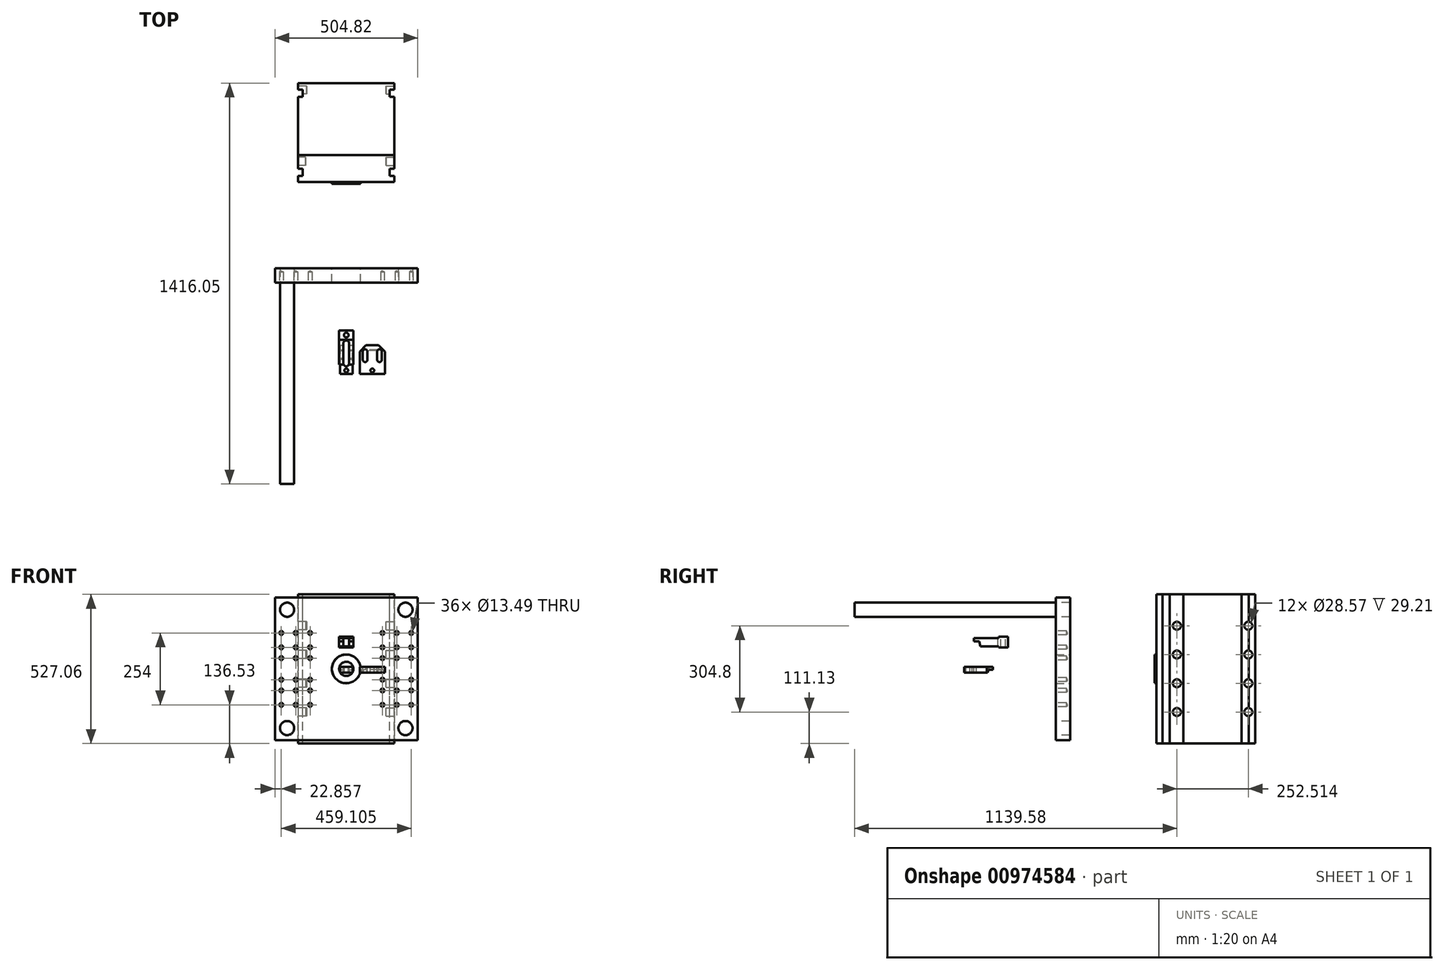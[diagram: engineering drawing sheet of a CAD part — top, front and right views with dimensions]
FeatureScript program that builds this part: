
annotation { "Feature Type Name" : "Feature", "Feature Type Description" : "" }
export const myFeature = defineFeature(function(context is Context, id is Id, definition is map)
    precondition{}
    {
        {
            var Q0;
            Q0=qCreatedBy(makeId("Front.planeOp"),FACE);
            var sketch = newSketch(context, id + "F0", { "sketchPlane" : qUnion([Q0])});
            skLineSegment(sketch, "E0.bottom", {"start": v(-252.41, 252.41) * mm, "end": v(252.41, 252.41) * mm});
            skLineSegment(sketch, "E0.top", {"start": v(-252.41, -252.41) * mm, "end": v(252.41, -252.41) * mm});
            skLineSegment(sketch, "E0.left", {"start": v(-252.41, 252.41) * mm, "end": v(-252.41, -252.41) * mm});
            skLineSegment(sketch, "E0.right", {"start": v(252.41, 252.41) * mm, "end": v(252.41, -252.41) * mm});
            skPoint(sketch, "E0.middle", {"position": v(0, 0) * mm});
            skSolve(sketch);
        }
        {
            var Q0;
            Q0=makeQuery(id+"F0.imprint","IMPRINT",FACE,{"disambiguationData":[TD([[makeQuery(id+"F0.imprint","IMPRINT",EDGE,{"derivedFrom":sQuery(id+"F0.wireOp",EDGE,"E0.bottom")}),-1.0]])]});
            extrude(context, id + "F1", {"entities" : qUnion([Q0]), "depth" : 50.8 * mm, "offsetDistance" : 25.4 * mm});
        }
        {
            var Q0;
            Q0=makeQuery(id+"F1.opExtrude","CAP_FACE",FACE,{"disambiguationData":[OSD([sQuery(id+"F0.wireOp",EDGE,"E0.bottom"),sQuery(id+"F0.wireOp",EDGE,"E0.top"),sQuery(id+"F0.wireOp",EDGE,"E0.left"),sQuery(id+"F0.wireOp",EDGE,"E0.right")])],"isStart":false});
            var sketch = newSketch(context, id + "F2", { "sketchPlane" : qUnion([Q0])});
            skLineSegment(sketch, "E1.bottom", {"start": v(-209.14, 209.14) * mm, "end": v(209.14, 209.14) * mm, "construction": true});
            skLineSegment(sketch, "E1.top", {"start": v(-209.14, -209.14) * mm, "end": v(209.14, -209.14) * mm, "construction": true});
            skLineSegment(sketch, "E1.left", {"start": v(-209.14, 209.14) * mm, "end": v(-209.14, -209.14) * mm, "construction": true});
            skLineSegment(sketch, "E1.right", {"start": v(209.14, 209.14) * mm, "end": v(209.14, -209.14) * mm, "construction": true});
            skPoint(sketch, "E1.middle", {"position": v(0, 0) * mm});
            skCircle(sketch, "E2", {"center": v(-209.14, 209.14) * mm, "radius": 25.02 * mm});
            skCircle(sketch, "E3", {"center": v(209.14, 209.14) * mm, "radius": 25.02 * mm});
            skCircle(sketch, "E4", {"center": v(209.14, -209.14) * mm, "radius": 25.02 * mm});
            skCircle(sketch, "E5", {"center": v(-209.14, -209.14) * mm, "radius": 25.02 * mm});
            skSolve(sketch);
        }
        {
            var Q0;
            Q0=makeQuery(id+"F2.imprint","IMPRINT",FACE,{"disambiguationData":[TD([[makeQuery(id+"F2.imprint","IMPRINT",EDGE,{"derivedFrom":sQuery(id+"F2.wireOp",EDGE,"E2")}),1.0]])]});
            var Q1;
            Q1=makeQuery(id+"F2.imprint","IMPRINT",FACE,{"disambiguationData":[TD([[makeQuery(id+"F2.imprint","IMPRINT",EDGE,{"derivedFrom":sQuery(id+"F2.wireOp",EDGE,"E3")}),1.0]])]});
            var Q2;
            Q2=makeQuery(id+"F2.imprint","IMPRINT",FACE,{"disambiguationData":[TD([[makeQuery(id+"F2.imprint","IMPRINT",EDGE,{"derivedFrom":sQuery(id+"F2.wireOp",EDGE,"E5")}),1.0]])]});
            var Q3;
            Q3=makeQuery(id+"F2.imprint","IMPRINT",FACE,{"disambiguationData":[TD([[makeQuery(id+"F2.imprint","IMPRINT",EDGE,{"derivedFrom":sQuery(id+"F2.wireOp",EDGE,"E4")}),1.0]])]});
            extrude(context, id + "F3", {"entities" : qUnion([Q0, Q1, Q2, Q3]), "operationType" : NewBodyOperationType.REMOVE, "endBound" : BoundingType.THROUGH_ALL, "oppositeDirection" : true, "depth" : 25.4 * mm, "offsetDistance" : 25.4 * mm});
        }
        {
            var Q0;
            Q0=makeQuery(id+"F1.opExtrude","CAP_FACE",FACE,{"disambiguationData":[OSD([sQuery(id+"F0.wireOp",EDGE,"E0.bottom"),sQuery(id+"F0.wireOp",EDGE,"E0.top"),sQuery(id+"F0.wireOp",EDGE,"E0.left"),sQuery(id+"F0.wireOp",EDGE,"E0.right")])],"isStart":false});
            var sketch = newSketch(context, id + "F4", { "sketchPlane" : qUnion([Q0])});
            skPoint(sketch, "E6", {"position": v(229.55, 38.1) * mm});
            skPoint(sketch, "E7", {"position": v(178.75, 38.1) * mm});
            skPoint(sketch, "E8", {"position": v(127.95, 38.1) * mm});
            skPoint(sketch, "E9", {"position": v(229.55, 76.2) * mm});
            skPoint(sketch, "E10", {"position": v(229.55, 127) * mm});
            skPoint(sketch, "E11", {"position": v(178.75, 76.2) * mm});
            skPoint(sketch, "E12", {"position": v(178.75, 127) * mm});
            skPoint(sketch, "E13", {"position": v(127.95, 76.2) * mm});
            skPoint(sketch, "E14", {"position": v(127.95, 127) * mm});
            skPoint(sketch, "E15.MirrorP", {"position": v(127.95, -38.1) * mm});
            skPoint(sketch, "E16.MirrorP", {"position": v(178.75, -38.1) * mm});
            skPoint(sketch, "E17.MirrorP", {"position": v(229.55, -38.1) * mm});
            skPoint(sketch, "E18.MirrorP", {"position": v(229.55, -76.2) * mm});
            skPoint(sketch, "E19.MirrorP", {"position": v(178.75, -76.2) * mm});
            skPoint(sketch, "E20.MirrorP", {"position": v(127.95, -76.2) * mm});
            skPoint(sketch, "E21.MirrorP", {"position": v(127.95, -127) * mm});
            skPoint(sketch, "E22.MirrorP", {"position": v(178.75, -127) * mm});
            skPoint(sketch, "E23.MirrorP", {"position": v(229.55, -127) * mm});
            skPoint(sketch, "E24.MirrorP", {"position": v(-127.95, -38.1) * mm});
            skPoint(sketch, "E25.MirrorP", {"position": v(-127.95, -76.2) * mm});
            skPoint(sketch, "E26.MirrorP", {"position": v(-127.95, -127) * mm});
            skPoint(sketch, "E27.MirrorP", {"position": v(-178.75, -127) * mm});
            skPoint(sketch, "E28.MirrorP", {"position": v(-178.75, -76.2) * mm});
            skPoint(sketch, "E29.MirrorP", {"position": v(-178.75, -38.1) * mm});
            skPoint(sketch, "E30.MirrorP", {"position": v(-229.55, -38.1) * mm});
            skPoint(sketch, "E31.MirrorP", {"position": v(-229.55, -76.2) * mm});
            skPoint(sketch, "E32.MirrorP", {"position": v(-229.55, -127) * mm});
            skPoint(sketch, "E33.MirrorP", {"position": v(-229.55, 38.1) * mm});
            skPoint(sketch, "E34.MirrorP", {"position": v(-229.55, 76.2) * mm});
            skPoint(sketch, "E35.MirrorP", {"position": v(-229.55, 127) * mm});
            skPoint(sketch, "E36.MirrorP", {"position": v(-178.75, 127) * mm});
            skPoint(sketch, "E37.MirrorP", {"position": v(-178.75, 76.2) * mm});
            skPoint(sketch, "E38.MirrorP", {"position": v(-178.75, 38.1) * mm});
            skPoint(sketch, "E39.MirrorP", {"position": v(-127.95, 38.1) * mm});
            skPoint(sketch, "E40.MirrorP", {"position": v(-127.95, 76.2) * mm});
            skPoint(sketch, "E41.MirrorP", {"position": v(-127.95, 127) * mm});
            skSolve(sketch);
        }
        {
            var Q0;
            Q0=sQuery(id+"F4.wireOp",VERTEX,"E35.MirrorP");
            var Q1;
            Q1=sQuery(id+"F4.wireOp",VERTEX,"E34.MirrorP");
            var Q2;
            Q2=sQuery(id+"F4.wireOp",VERTEX,"E33.MirrorP");
            var Q3;
            Q3=sQuery(id+"F4.wireOp",VERTEX,"E38.MirrorP");
            var Q4;
            Q4=sQuery(id+"F4.wireOp",VERTEX,"E37.MirrorP");
            var Q5;
            Q5=sQuery(id+"F4.wireOp",VERTEX,"E36.MirrorP");
            var Q6;
            Q6=sQuery(id+"F4.wireOp",VERTEX,"E41.MirrorP");
            var Q7;
            Q7=sQuery(id+"F4.wireOp",VERTEX,"E40.MirrorP");
            var Q8;
            Q8=sQuery(id+"F4.wireOp",VERTEX,"E39.MirrorP");
            var Q9;
            Q9=sQuery(id+"F4.wireOp",VERTEX,"E24.MirrorP");
            var Q10;
            Q10=sQuery(id+"F4.wireOp",VERTEX,"E29.MirrorP");
            var Q11;
            Q11=sQuery(id+"F4.wireOp",VERTEX,"E30.MirrorP");
            var Q12;
            Q12=sQuery(id+"F4.wireOp",VERTEX,"E31.MirrorP");
            var Q13;
            Q13=sQuery(id+"F4.wireOp",VERTEX,"E28.MirrorP");
            var Q14;
            Q14=sQuery(id+"F4.wireOp",VERTEX,"E25.MirrorP");
            var Q15;
            Q15=sQuery(id+"F4.wireOp",VERTEX,"E26.MirrorP");
            var Q16;
            Q16=sQuery(id+"F4.wireOp",VERTEX,"E27.MirrorP");
            var Q17;
            Q17=sQuery(id+"F4.wireOp",VERTEX,"E32.MirrorP");
            var Q18;
            Q18=sQuery(id+"F4.wireOp",VERTEX,"E21.MirrorP");
            var Q19;
            Q19=sQuery(id+"F4.wireOp",VERTEX,"E22.MirrorP");
            var Q20;
            Q20=sQuery(id+"F4.wireOp",VERTEX,"E23.MirrorP");
            var Q21;
            Q21=sQuery(id+"F4.wireOp",VERTEX,"E18.MirrorP");
            var Q22;
            Q22=sQuery(id+"F4.wireOp",VERTEX,"E19.MirrorP");
            var Q23;
            Q23=sQuery(id+"F4.wireOp",VERTEX,"E20.MirrorP");
            var Q24;
            Q24=sQuery(id+"F4.wireOp",VERTEX,"E15.MirrorP");
            var Q25;
            Q25=sQuery(id+"F4.wireOp",VERTEX,"E16.MirrorP");
            var Q26;
            Q26=sQuery(id+"F4.wireOp",VERTEX,"E17.MirrorP");
            var Q27;
            Q27=sQuery(id+"F4.wireOp",VERTEX,"E6");
            var Q28;
            Q28=sQuery(id+"F4.wireOp",VERTEX,"E7");
            var Q29;
            Q29=sQuery(id+"F4.wireOp",VERTEX,"E8");
            var Q30;
            Q30=sQuery(id+"F4.wireOp",VERTEX,"E13");
            var Q31;
            Q31=sQuery(id+"F4.wireOp",VERTEX,"E11");
            var Q32;
            Q32=sQuery(id+"F4.wireOp",VERTEX,"E9");
            var Q33;
            Q33=sQuery(id+"F4.wireOp",VERTEX,"E10");
            var Q34;
            Q34=sQuery(id+"F4.wireOp",VERTEX,"E12");
            var Q35;
            Q35=sQuery(id+"F4.wireOp",VERTEX,"E14");
            var Q36;
            Q36=makeQuery(id+"F1.opExtrude","SWEPT_BODY",BODY,{"disambiguationData":[OSD([sQuery(id+"F0.wireOp",EDGE,"E0.bottom"),sQuery(id+"F0.wireOp",EDGE,"E0.top"),sQuery(id+"F0.wireOp",EDGE,"E0.left"),sQuery(id+"F0.wireOp",EDGE,"E0.right")])]});
            hole(context, id + "F5", {"style" : HoleStyle.SIMPLE, "endStyle" : HoleEndStyle.BLIND, "standardTappedOrClearance" : lookupTablePath({ "standard" : "ANSI", "engagement" : "75%", "pitch" : "11 tpi", "size" : "5/8", "type" : "Tapped" }), "standardBlindInLast" : lookupTablePath({ "standard" : "ANSI", "fit" : "Free", "engagement" : "75%", "pitch" : "11 tpi", "size" : "5/8", "type" : "Clearance & tapped" }), "holeDiameter" : 13.5 * mm, "majorDiameter" : 15.88 * mm, "showTappedDepth" : true, "holeDepth" : 38.1 * mm, "isTappedThrough" : true, "tappedDepth" : 31.17 * mm, "tapClearance" : 3, "startFromSketch" : true, "locations" : qUnion([Q0, Q1, Q2, Q3, Q4, Q5, Q6, Q7, Q8, Q9, Q10, Q11, Q12, Q13, Q14, Q15, Q16, Q17, Q18, Q19, Q20, Q21, Q22, Q23, Q24, Q25, Q26, Q27, Q28, Q29, Q30, Q31, Q32, Q33, Q34, Q35]), "scope" : qUnion([Q36])});
        }
        {
            var Q0;
            Q0=makeQuery(id+"F1.opExtrude","CAP_FACE",FACE,{"disambiguationData":[OSD([sQuery(id+"F0.wireOp",EDGE,"E0.bottom"),sQuery(id+"F0.wireOp",EDGE,"E0.top"),sQuery(id+"F0.wireOp",EDGE,"E0.left"),sQuery(id+"F0.wireOp",EDGE,"E0.right")])],"isStart":false});
            var sketch = newSketch(context, id + "F6", { "sketchPlane" : qUnion([Q0])});
            skCircle(sketch, "E42.0", {"center": v(-209.14, 209.14) * mm, "radius": 25.02 * mm});
            skSolve(sketch);
        }
        {
            var Q0;
            Q0=makeQuery(id+"F6.imprint","IMPRINT",FACE,{"disambiguationData":[TD([[makeQuery(id+"F6.imprint","IMPRINT",EDGE,{"derivedFrom":sQuery(id+"F6.wireOp",EDGE,"E42.0")}),1.0]])]});
            extrude(context, id + "F7", {"entities" : qUnion([Q0]), "depth" : 711.2 * mm, "offsetDistance" : 25.4 * mm});
        }
        {
            var Q0;
            Q0=qCreatedBy(makeId("Right.planeOp"),FACE);
            var sketch = newSketch(context, id + "F8", { "sketchPlane" : qUnion([Q0])});
            skLineSegment(sketch, "E43.bottom", {"start": v(304.8, 263.53) * mm, "end": v(400.05, 263.53) * mm});
            skLineSegment(sketch, "E43.top", {"start": v(304.8, -263.52) * mm, "end": v(400.05, -263.52) * mm});
            skLineSegment(sketch, "E43.left", {"start": v(304.8, 263.53) * mm, "end": v(304.8, -263.52) * mm});
            skLineSegment(sketch, "E43.right", {"start": v(400.05, 263.53) * mm, "end": v(400.05, -263.52) * mm});
            skPoint(sketch, "E43.middle", {"position": v(352.43, 0) * mm});
            skSolve(sketch);
        }
        {
            var Q0;
            Q0=makeQuery(id+"F8.imprint","IMPRINT",FACE,{"disambiguationData":[TD([[makeQuery(id+"F8.imprint","IMPRINT",EDGE,{"derivedFrom":sQuery(id+"F8.wireOp",EDGE,"E43.bottom")}),-1.0]])]});
            extrude(context, id + "F9", {"entities" : qUnion([Q0]), "endBound" : BoundingType.SYMMETRIC, "depth" : 339.72 * mm, "offsetDistance" : 25.4 * mm});
        }
        {
            var Q0;
            Q0=makeQuery(id+"F9.opExtrude","SWEPT_FACE",FACE,{"disambiguationData":[OSD([sQuery(id+"F8.wireOp",EDGE,"E43.bottom")])]});
            var sketch = newSketch(context, id + "F10", { "sketchPlane" : qUnion([Q0])});
            skLineSegment(sketch, "E44.bottom", {"start": v(169.86, 327.03) * mm, "end": v(153.86, 327.03) * mm});
            skLineSegment(sketch, "E44.top", {"start": v(169.86, 352.43) * mm, "end": v(153.86, 352.43) * mm});
            skLineSegment(sketch, "E44.left", {"start": v(169.86, 327.03) * mm, "end": v(169.86, 352.43) * mm});
            skLineSegment(sketch, "E44.right", {"start": v(153.86, 327.03) * mm, "end": v(153.86, 352.43) * mm});
            skLineSegment(sketch, "E45", {"start": v(0, 400.05) * mm, "end": v(0, 304.8) * mm, "construction": true});
            skLineSegment(sketch, "E46.MirrorCS", {"start": v(-153.86, 327.03) * mm, "end": v(-153.86, 352.43) * mm});
            skLineSegment(sketch, "E47.MirrorCS", {"start": v(-169.86, 352.43) * mm, "end": v(-153.86, 352.43) * mm});
            skLineSegment(sketch, "E48.MirrorCS", {"start": v(-169.86, 327.03) * mm, "end": v(-169.86, 352.43) * mm});
            skLineSegment(sketch, "E49.MirrorCS", {"start": v(-169.86, 327.03) * mm, "end": v(-153.86, 327.03) * mm});
            skSolve(sketch);
        }
        {
            var Q0;
            Q0=makeQuery(id+"F10.imprint","IMPRINT",FACE,{"disambiguationData":[TD([[makeQuery(id+"F10.imprint","IMPRINT",EDGE,{"derivedFrom":sQuery(id+"F10.wireOp",EDGE,"E46.MirrorCS")}),1.0]])]});
            var Q1;
            Q1=makeQuery(id+"F10.imprint","IMPRINT",FACE,{"disambiguationData":[TD([[makeQuery(id+"F10.imprint","IMPRINT",EDGE,{"derivedFrom":sQuery(id+"F10.wireOp",EDGE,"E44.bottom")}),-1.0]])]});
            extrude(context, id + "F11", {"entities" : qUnion([Q0, Q1]), "operationType" : NewBodyOperationType.REMOVE, "endBound" : BoundingType.THROUGH_ALL, "oppositeDirection" : true, "depth" : 25.4 * mm, "offsetDistance" : 25.4 * mm});
        }
        {
            var Q0;
            {var subQ0=sQuery(id+"F8.wireOp",EDGE,"E43.bottom");var subQ1=sQuery(id+"F8.wireOp",EDGE,"E43.right");var subQ2=sQuery(id+"F8.wireOp",EDGE,"E43.top");Q0=makeQuery(id+"F11.boolean.opBoolean","SPLIT",FACE,{"disambiguationData":[TD([makeQuery(id+"F9.opExtrude","SWEPT_FACE",FACE,{"disambiguationData":[OSD([subQ1])]})])],"derivedFrom":makeQuery(id+"F9.opExtrude","CAP_FACE",FACE,{"disambiguationData":[OSD([subQ0,subQ2,sQuery(id+"F8.wireOp",EDGE,"E43.left"),subQ1])],"isStart":false})});}
            var sketch = newSketch(context, id + "F12", { "sketchPlane" : qUnion([Q0])});
            skCircle(sketch, "E50", {"center": v(377.58, 152.4) * mm, "radius": 14.29 * mm});
            skCircle(sketch, "E51", {"center": v(377.58, 50.8) * mm, "radius": 14.29 * mm});
            skCircle(sketch, "E52", {"center": v(377.58, -50.8) * mm, "radius": 14.29 * mm});
            skCircle(sketch, "E53", {"center": v(377.58, -152.4) * mm, "radius": 14.29 * mm});
            skLineSegment(sketch, "E54", {"start": v(377.58, 50.8) * mm, "end": v(377.58, -50.8) * mm, "construction": true});
            skPoint(sketch, "E55", {"position": v(377.58, 0) * mm});
            skSolve(sketch);
        }
        {
            var Q0;
            Q0=makeQuery(id+"F12.imprint","IMPRINT",FACE,{"disambiguationData":[TD([[makeQuery(id+"F12.imprint","IMPRINT",EDGE,{"derivedFrom":sQuery(id+"F12.wireOp",EDGE,"E50")}),1.0]])]});
            var Q1;
            Q1=makeQuery(id+"F12.imprint","IMPRINT",FACE,{"disambiguationData":[TD([[makeQuery(id+"F12.imprint","IMPRINT",EDGE,{"derivedFrom":sQuery(id+"F12.wireOp",EDGE,"E51")}),1.0]])]});
            var Q2;
            Q2=makeQuery(id+"F12.imprint","IMPRINT",FACE,{"disambiguationData":[TD([[makeQuery(id+"F12.imprint","IMPRINT",EDGE,{"derivedFrom":sQuery(id+"F12.wireOp",EDGE,"E52")}),1.0]])]});
            var Q3;
            Q3=makeQuery(id+"F12.imprint","IMPRINT",FACE,{"disambiguationData":[TD([[makeQuery(id+"F12.imprint","IMPRINT",EDGE,{"derivedFrom":sQuery(id+"F12.wireOp",EDGE,"E53")}),1.0]])]});
            extrude(context, id + "F13", {"entities" : qUnion([Q0, Q1, Q2, Q3]), "operationType" : NewBodyOperationType.REMOVE, "oppositeDirection" : true, "depth" : 29.2 * mm, "offsetDistance" : 25.4 * mm});
        }
        {
            var Q0;
            {var subQ0=sQuery(id+"F8.wireOp",EDGE,"E43.bottom");var subQ1=sQuery(id+"F8.wireOp",EDGE,"E43.right");var subQ2=sQuery(id+"F8.wireOp",EDGE,"E43.top");Q0=makeQuery(id+"F11.boolean.opBoolean","SPLIT",FACE,{"disambiguationData":[TD([makeQuery(id+"F9.opExtrude","SWEPT_FACE",FACE,{"disambiguationData":[OSD([subQ1])]})])],"derivedFrom":makeQuery(id+"F9.opExtrude","CAP_FACE",FACE,{"disambiguationData":[OSD([subQ0,subQ2,sQuery(id+"F8.wireOp",EDGE,"E43.left"),subQ1])],"isStart":true})});}
            var sketch = newSketch(context, id + "F14", { "sketchPlane" : qUnion([Q0])});
            skCircle(sketch, "E56.0", {"center": v(-377.58, 152.4) * mm, "radius": 14.29 * mm});
            skCircle(sketch, "E57.0", {"center": v(-377.58, 50.8) * mm, "radius": 14.29 * mm});
            skCircle(sketch, "E58.0", {"center": v(-377.58, -50.8) * mm, "radius": 14.29 * mm});
            skCircle(sketch, "E59.0", {"center": v(-377.58, -152.4) * mm, "radius": 14.29 * mm});
            skSolve(sketch);
        }
        {
            var Q0;
            Q0=makeQuery(id+"F14.imprint","IMPRINT",FACE,{"disambiguationData":[TD([[makeQuery(id+"F14.imprint","IMPRINT",EDGE,{"derivedFrom":sQuery(id+"F14.wireOp",EDGE,"E56.0")}),1.0]])]});
            var Q1;
            Q1=makeQuery(id+"F14.imprint","IMPRINT",FACE,{"disambiguationData":[TD([[makeQuery(id+"F14.imprint","IMPRINT",EDGE,{"derivedFrom":sQuery(id+"F14.wireOp",EDGE,"E57.0")}),1.0]])]});
            var Q2;
            Q2=makeQuery(id+"F14.imprint","IMPRINT",FACE,{"disambiguationData":[TD([[makeQuery(id+"F14.imprint","IMPRINT",EDGE,{"derivedFrom":sQuery(id+"F14.wireOp",EDGE,"E58.0")}),1.0]])]});
            var Q3;
            Q3=makeQuery(id+"F14.imprint","IMPRINT",FACE,{"disambiguationData":[TD([[makeQuery(id+"F14.imprint","IMPRINT",EDGE,{"derivedFrom":sQuery(id+"F14.wireOp",EDGE,"E59.0")}),1.0]])]});
            extrude(context, id + "F15", {"entities" : qUnion([Q0, Q1, Q2, Q3]), "operationType" : NewBodyOperationType.REMOVE, "oppositeDirection" : true, "depth" : 25.4 * mm, "offsetDistance" : 25.4 * mm});
        }
        {
            var Q0;
            Q0=makeQuery(id+"F9.opExtrude","SWEPT_FACE",FACE,{"disambiguationData":[OSD([sQuery(id+"F8.wireOp",EDGE,"E43.left")])]});
            var sketch = newSketch(context, id + "F16", { "sketchPlane" : qUnion([Q0])});
            skCircle(sketch, "E60", {"center": v(0, 0) * mm, "radius": 50.62 * mm});
            skCircle(sketch, "E61", {"center": v(0, 0) * mm, "radius": 25.17 * mm});
            skSolve(sketch);
        }
        {
            var Q0;
            Q0=makeQuery(id+"F16.imprint","IMPRINT",FACE,{"disambiguationData":[TD([[makeQuery(id+"F16.imprint","IMPRINT",EDGE,{"derivedFrom":sQuery(id+"F16.wireOp",EDGE,"E60")}),1.0]])]});
            extrude(context, id + "F17", {"entities" : qUnion([Q0]), "operationType" : NewBodyOperationType.ADD, "depth" : 6.35 * mm, "offsetDistance" : 25.4 * mm});
        }
        {
            var Q0;
            Q0=makeQuery(id+"F9.opExtrude","SWEPT_FACE",FACE,{"disambiguationData":[OSD([sQuery(id+"F8.wireOp",EDGE,"E43.right")])]});
            var sketch = newSketch(context, id + "F18", { "sketchPlane" : qUnion([Q0])});
            skLineSegment(sketch, "E62.bottom", {"start": v(-169.86, 263.53) * mm, "end": v(169.86, 263.53) * mm});
            skLineSegment(sketch, "E62.top", {"start": v(-169.86, -263.52) * mm, "end": v(169.86, -263.52) * mm});
            skLineSegment(sketch, "E62.left", {"start": v(-169.86, 263.53) * mm, "end": v(-169.86, -263.52) * mm});
            skLineSegment(sketch, "E62.right", {"start": v(169.86, 263.53) * mm, "end": v(169.86, -263.52) * mm});
            skSolve(sketch);
        }
        {
            var Q0;
            Q0=makeQuery(id+"F18.imprint","IMPRINT",FACE,{"disambiguationData":[TD([[makeQuery(id+"F18.imprint","IMPRINT",EDGE,{"derivedFrom":sQuery(id+"F18.wireOp",EDGE,"E62.bottom")}),-1.0]])]});
            extrude(context, id + "F19", {"entities" : qUnion([Q0]), "depth" : 254 * mm, "offsetDistance" : 25.4 * mm});
        }
        {
            var Q0;
            Q0=makeQuery(id+"F19.opExtrude","SWEPT_FACE",FACE,{"disambiguationData":[OSD([sQuery(id+"F18.wireOp",EDGE,"E62.bottom")])]});
            var sketch = newSketch(context, id + "F20", { "sketchPlane" : qUnion([Q0])});
            skLineSegment(sketch, "E63.bottom", {"start": v(169.86, 631.82) * mm, "end": v(153.86, 631.82) * mm});
            skLineSegment(sketch, "E63.top", {"start": v(169.86, 606.42) * mm, "end": v(153.86, 606.42) * mm});
            skLineSegment(sketch, "E63.left", {"start": v(169.86, 631.82) * mm, "end": v(169.86, 606.42) * mm});
            skLineSegment(sketch, "E63.right", {"start": v(153.86, 631.82) * mm, "end": v(153.86, 606.42) * mm});
            skLineSegment(sketch, "E64.bottom", {"start": v(-169.86, 631.82) * mm, "end": v(-153.86, 631.82) * mm});
            skLineSegment(sketch, "E64.top", {"start": v(-169.86, 606.42) * mm, "end": v(-153.86, 606.42) * mm});
            skLineSegment(sketch, "E64.left", {"start": v(-169.86, 631.82) * mm, "end": v(-169.86, 606.42) * mm});
            skLineSegment(sketch, "E64.right", {"start": v(-153.86, 631.82) * mm, "end": v(-153.86, 606.42) * mm});
            skSolve(sketch);
        }
        {
            var Q0;
            Q0=makeQuery(id+"F20.imprint","IMPRINT",FACE,{"disambiguationData":[TD([[makeQuery(id+"F20.imprint","IMPRINT",EDGE,{"derivedFrom":sQuery(id+"F20.wireOp",EDGE,"E64.bottom")}),-1.0]])]});
            var Q1;
            Q1=makeQuery(id+"F20.imprint","IMPRINT",FACE,{"disambiguationData":[TD([[makeQuery(id+"F20.imprint","IMPRINT",EDGE,{"derivedFrom":sQuery(id+"F20.wireOp",EDGE,"E63.bottom")}),1.0]])]});
            extrude(context, id + "F21", {"entities" : qUnion([Q0, Q1]), "operationType" : NewBodyOperationType.REMOVE, "endBound" : BoundingType.THROUGH_ALL, "oppositeDirection" : true, "depth" : 25.4 * mm, "offsetDistance" : 25.4 * mm});
        }
        {
            var Q0;
            {var subQ1=sQuery(id+"F18.wireOp",EDGE,"E62.left");Q0=makeQuery(id+"F21.boolean.opBoolean","SPLIT",FACE,{"disambiguationData":[TD([makeQuery(id+"F21.opExtrude","SWEPT_FACE",FACE,{"disambiguationData":[OSD([sQuery(id+"F20.wireOp",EDGE,"E63.bottom")])]})])],"derivedFrom":makeQuery(id+"F19.opExtrude","SWEPT_FACE",FACE,{"disambiguationData":[OSD([subQ1])]})});}
            var sketch = newSketch(context, id + "F22", { "sketchPlane" : qUnion([Q0])});
            skCircle(sketch, "E65", {"center": v(630.1, 152.4) * mm, "radius": 14.29 * mm});
            skCircle(sketch, "E66", {"center": v(630.1, 50.8) * mm, "radius": 14.29 * mm});
            skCircle(sketch, "E67", {"center": v(630.1, -50.8) * mm, "radius": 14.29 * mm});
            skCircle(sketch, "E68", {"center": v(630.1, -152.4) * mm, "radius": 14.29 * mm});
            skCircle(sketch, "E69.0", {"center": v(377.58, 50.8) * mm, "radius": 14.29 * mm});
            skCircle(sketch, "E70.0", {"center": v(377.58, 152.4) * mm, "radius": 14.29 * mm});
            skCircle(sketch, "E71.0", {"center": v(377.58, -50.8) * mm, "radius": 14.29 * mm});
            skCircle(sketch, "E72.0", {"center": v(377.58, -152.4) * mm, "radius": 14.29 * mm});
            skSolve(sketch);
        }
        {
            var Q0;
            {var subQ0=sQuery(id+"F22.wireOp",EDGE,"E65");var subQ1=makeQuery(id+"F21.boolean.opBoolean","COPY",EDGE,{"derivedFrom":makeQuery(id+"F21.opExtrude","SWEPT_EDGE",EDGE,{"disambiguationData":[OSD([sQuery(id+"F18.wireOp",EDGE,"E62.bottom"),sQuery(id+"F18.wireOp",EDGE,"E62.left"),sQuery(id+"F20.wireOp",EDGE,"E63.bottom"),sQuery(id+"F20.wireOp",EDGE,"E63.left")])]})});var subQ2=makeQuery(id+"F22.imprint","INTERSECT",VERTEX,{"disambiguationData":[OD(0.0)],"derivedFrom":[subQ1,subQ0]});Q0=makeQuery(id+"F22.imprint","IMPRINT",FACE,{"disambiguationData":[TD([[makeQuery(id+"F22.imprint","IMPRINT",EDGE,{"disambiguationData":[TD([[subQ2,1.0]])],"derivedFrom":subQ0}),1.0]])]});}
            var Q1;
            {var subQ0=sQuery(id+"F22.wireOp",EDGE,"E65");var subQ1=makeQuery(id+"F21.boolean.opBoolean","COPY",EDGE,{"derivedFrom":makeQuery(id+"F21.opExtrude","SWEPT_EDGE",EDGE,{"disambiguationData":[OSD([sQuery(id+"F18.wireOp",EDGE,"E62.bottom"),sQuery(id+"F18.wireOp",EDGE,"E62.left"),sQuery(id+"F20.wireOp",EDGE,"E63.bottom"),sQuery(id+"F20.wireOp",EDGE,"E63.left")])]})});var subQ2=makeQuery(id+"F22.imprint","INTERSECT",VERTEX,{"disambiguationData":[OD(0.0)],"derivedFrom":[subQ1,subQ0]});Q1=makeQuery(id+"F22.imprint","IMPRINT",FACE,{"disambiguationData":[TD([[makeQuery(id+"F22.imprint","IMPRINT",EDGE,{"disambiguationData":[TD([[subQ2,-1.0]])],"derivedFrom":subQ0}),1.0]])]});}
            var Q2;
            {var subQ0=sQuery(id+"F22.wireOp",EDGE,"E66");var subQ1=makeQuery(id+"F21.boolean.opBoolean","COPY",EDGE,{"derivedFrom":makeQuery(id+"F21.opExtrude","SWEPT_EDGE",EDGE,{"disambiguationData":[OSD([sQuery(id+"F18.wireOp",EDGE,"E62.bottom"),sQuery(id+"F18.wireOp",EDGE,"E62.left"),sQuery(id+"F20.wireOp",EDGE,"E63.bottom"),sQuery(id+"F20.wireOp",EDGE,"E63.left")])]})});var subQ2=makeQuery(id+"F22.imprint","INTERSECT",VERTEX,{"disambiguationData":[OD(0.0)],"derivedFrom":[subQ1,subQ0]});Q2=makeQuery(id+"F22.imprint","IMPRINT",FACE,{"disambiguationData":[TD([[makeQuery(id+"F22.imprint","IMPRINT",EDGE,{"disambiguationData":[TD([[subQ2,-1.0]])],"derivedFrom":subQ0}),1.0]])]});}
            var Q3;
            {var subQ0=sQuery(id+"F22.wireOp",EDGE,"E66");var subQ1=makeQuery(id+"F21.boolean.opBoolean","COPY",EDGE,{"derivedFrom":makeQuery(id+"F21.opExtrude","SWEPT_EDGE",EDGE,{"disambiguationData":[OSD([sQuery(id+"F18.wireOp",EDGE,"E62.bottom"),sQuery(id+"F18.wireOp",EDGE,"E62.left"),sQuery(id+"F20.wireOp",EDGE,"E63.bottom"),sQuery(id+"F20.wireOp",EDGE,"E63.left")])]})});var subQ2=makeQuery(id+"F22.imprint","INTERSECT",VERTEX,{"disambiguationData":[OD(0.0)],"derivedFrom":[subQ1,subQ0]});Q3=makeQuery(id+"F22.imprint","IMPRINT",FACE,{"disambiguationData":[TD([[makeQuery(id+"F22.imprint","IMPRINT",EDGE,{"disambiguationData":[TD([[subQ2,1.0]])],"derivedFrom":subQ0}),1.0]])]});}
            var Q4;
            {var subQ0=sQuery(id+"F22.wireOp",EDGE,"E67");var subQ1=makeQuery(id+"F21.boolean.opBoolean","COPY",EDGE,{"derivedFrom":makeQuery(id+"F21.opExtrude","SWEPT_EDGE",EDGE,{"disambiguationData":[OSD([sQuery(id+"F18.wireOp",EDGE,"E62.bottom"),sQuery(id+"F18.wireOp",EDGE,"E62.left"),sQuery(id+"F20.wireOp",EDGE,"E63.bottom"),sQuery(id+"F20.wireOp",EDGE,"E63.left")])]})});var subQ2=makeQuery(id+"F22.imprint","INTERSECT",VERTEX,{"disambiguationData":[OD(0.0)],"derivedFrom":[subQ1,subQ0]});Q4=makeQuery(id+"F22.imprint","IMPRINT",FACE,{"disambiguationData":[TD([[makeQuery(id+"F22.imprint","IMPRINT",EDGE,{"disambiguationData":[TD([[subQ2,1.0]])],"derivedFrom":subQ0}),1.0]])]});}
            var Q5;
            {var subQ0=sQuery(id+"F22.wireOp",EDGE,"E67");var subQ1=makeQuery(id+"F21.boolean.opBoolean","COPY",EDGE,{"derivedFrom":makeQuery(id+"F21.opExtrude","SWEPT_EDGE",EDGE,{"disambiguationData":[OSD([sQuery(id+"F18.wireOp",EDGE,"E62.bottom"),sQuery(id+"F18.wireOp",EDGE,"E62.left"),sQuery(id+"F20.wireOp",EDGE,"E63.bottom"),sQuery(id+"F20.wireOp",EDGE,"E63.left")])]})});var subQ2=makeQuery(id+"F22.imprint","INTERSECT",VERTEX,{"disambiguationData":[OD(0.0)],"derivedFrom":[subQ1,subQ0]});Q5=makeQuery(id+"F22.imprint","IMPRINT",FACE,{"disambiguationData":[TD([[makeQuery(id+"F22.imprint","IMPRINT",EDGE,{"disambiguationData":[TD([[subQ2,-1.0]])],"derivedFrom":subQ0}),1.0]])]});}
            var Q6;
            {var subQ0=sQuery(id+"F22.wireOp",EDGE,"E68");var subQ1=makeQuery(id+"F21.boolean.opBoolean","COPY",EDGE,{"derivedFrom":makeQuery(id+"F21.opExtrude","SWEPT_EDGE",EDGE,{"disambiguationData":[OSD([sQuery(id+"F18.wireOp",EDGE,"E62.bottom"),sQuery(id+"F18.wireOp",EDGE,"E62.left"),sQuery(id+"F20.wireOp",EDGE,"E63.bottom"),sQuery(id+"F20.wireOp",EDGE,"E63.left")])]})});var subQ2=makeQuery(id+"F22.imprint","INTERSECT",VERTEX,{"disambiguationData":[OD(0.0)],"derivedFrom":[subQ1,subQ0]});Q6=makeQuery(id+"F22.imprint","IMPRINT",FACE,{"disambiguationData":[TD([[makeQuery(id+"F22.imprint","IMPRINT",EDGE,{"disambiguationData":[TD([[subQ2,1.0]])],"derivedFrom":subQ0}),1.0]])]});}
            var Q7;
            {var subQ0=sQuery(id+"F22.wireOp",EDGE,"E68");var subQ1=makeQuery(id+"F21.boolean.opBoolean","COPY",EDGE,{"derivedFrom":makeQuery(id+"F21.opExtrude","SWEPT_EDGE",EDGE,{"disambiguationData":[OSD([sQuery(id+"F18.wireOp",EDGE,"E62.bottom"),sQuery(id+"F18.wireOp",EDGE,"E62.left"),sQuery(id+"F20.wireOp",EDGE,"E63.bottom"),sQuery(id+"F20.wireOp",EDGE,"E63.left")])]})});var subQ2=makeQuery(id+"F22.imprint","INTERSECT",VERTEX,{"disambiguationData":[OD(0.0)],"derivedFrom":[subQ1,subQ0]});Q7=makeQuery(id+"F22.imprint","IMPRINT",FACE,{"disambiguationData":[TD([[makeQuery(id+"F22.imprint","IMPRINT",EDGE,{"disambiguationData":[TD([[subQ2,-1.0]])],"derivedFrom":subQ0}),1.0]])]});}
            extrude(context, id + "F23", {"entities" : qUnion([Q0, Q1, Q2, Q3, Q4, Q5, Q6, Q7]), "operationType" : NewBodyOperationType.REMOVE, "oppositeDirection" : true, "depth" : 29.2 * mm, "offsetDistance" : 25.4 * mm});
        }
        {
            var Q0;
            {var subQ1=sQuery(id+"F18.wireOp",EDGE,"E62.right");Q0=makeQuery(id+"F21.boolean.opBoolean","SPLIT",FACE,{"disambiguationData":[TD([makeQuery(id+"F21.opExtrude","SWEPT_FACE",FACE,{"disambiguationData":[OSD([sQuery(id+"F20.wireOp",EDGE,"E64.bottom")])]})])],"derivedFrom":makeQuery(id+"F19.opExtrude","SWEPT_FACE",FACE,{"disambiguationData":[OSD([subQ1])]})});}
            var sketch = newSketch(context, id + "F24", { "sketchPlane" : qUnion([Q0])});
            skCircle(sketch, "E73.0.0", {"center": v(-630.1, 152.4) * mm, "radius": 14.29 * mm});
            skCircle(sketch, "E74.0.0", {"center": v(-630.1, 50.8) * mm, "radius": 14.29 * mm});
            skCircle(sketch, "E75.0.0", {"center": v(-630.1, -50.8) * mm, "radius": 14.29 * mm});
            skCircle(sketch, "E76.0.0", {"center": v(-630.1, -152.4) * mm, "radius": 14.29 * mm});
            skSolve(sketch);
        }
        {
            var Q0;
            {var subQ0=sQuery(id+"F24.wireOp",EDGE,"E73.0.0");var subQ1=makeQuery(id+"F21.boolean.opBoolean","COPY",EDGE,{"derivedFrom":makeQuery(id+"F21.opExtrude","SWEPT_EDGE",EDGE,{"disambiguationData":[OSD([sQuery(id+"F18.wireOp",EDGE,"E62.bottom"),sQuery(id+"F18.wireOp",EDGE,"E62.right"),sQuery(id+"F20.wireOp",EDGE,"E64.bottom"),sQuery(id+"F20.wireOp",EDGE,"E64.left")])]})});var subQ2=makeQuery(id+"F24.imprint","INTERSECT",VERTEX,{"disambiguationData":[OD(0.0)],"derivedFrom":[subQ1,subQ0]});Q0=makeQuery(id+"F24.imprint","IMPRINT",FACE,{"disambiguationData":[TD([[makeQuery(id+"F24.imprint","IMPRINT",EDGE,{"disambiguationData":[TD([[subQ2,-1.0]])],"derivedFrom":subQ0}),1.0]])]});}
            var Q1;
            {var subQ0=sQuery(id+"F24.wireOp",EDGE,"E74.0.0");var subQ1=makeQuery(id+"F21.boolean.opBoolean","COPY",EDGE,{"derivedFrom":makeQuery(id+"F21.opExtrude","SWEPT_EDGE",EDGE,{"disambiguationData":[OSD([sQuery(id+"F18.wireOp",EDGE,"E62.bottom"),sQuery(id+"F18.wireOp",EDGE,"E62.right"),sQuery(id+"F20.wireOp",EDGE,"E64.bottom"),sQuery(id+"F20.wireOp",EDGE,"E64.left")])]})});var subQ2=makeQuery(id+"F24.imprint","INTERSECT",VERTEX,{"disambiguationData":[OD(0.0)],"derivedFrom":[subQ1,subQ0]});Q1=makeQuery(id+"F24.imprint","IMPRINT",FACE,{"disambiguationData":[TD([[makeQuery(id+"F24.imprint","IMPRINT",EDGE,{"disambiguationData":[TD([[subQ2,-1.0]])],"derivedFrom":subQ0}),1.0]])]});}
            var Q2;
            {var subQ0=sQuery(id+"F24.wireOp",EDGE,"E74.0.0");var subQ1=makeQuery(id+"F21.boolean.opBoolean","COPY",EDGE,{"derivedFrom":makeQuery(id+"F21.opExtrude","SWEPT_EDGE",EDGE,{"disambiguationData":[OSD([sQuery(id+"F18.wireOp",EDGE,"E62.bottom"),sQuery(id+"F18.wireOp",EDGE,"E62.right"),sQuery(id+"F20.wireOp",EDGE,"E64.bottom"),sQuery(id+"F20.wireOp",EDGE,"E64.left")])]})});var subQ2=makeQuery(id+"F24.imprint","INTERSECT",VERTEX,{"disambiguationData":[OD(0.0)],"derivedFrom":[subQ1,subQ0]});Q2=makeQuery(id+"F24.imprint","IMPRINT",FACE,{"disambiguationData":[TD([[makeQuery(id+"F24.imprint","IMPRINT",EDGE,{"disambiguationData":[TD([[subQ2,1.0]])],"derivedFrom":subQ0}),1.0]])]});}
            var Q3;
            {var subQ0=sQuery(id+"F24.wireOp",EDGE,"E73.0.0");var subQ1=makeQuery(id+"F21.boolean.opBoolean","COPY",EDGE,{"derivedFrom":makeQuery(id+"F21.opExtrude","SWEPT_EDGE",EDGE,{"disambiguationData":[OSD([sQuery(id+"F18.wireOp",EDGE,"E62.bottom"),sQuery(id+"F18.wireOp",EDGE,"E62.right"),sQuery(id+"F20.wireOp",EDGE,"E64.bottom"),sQuery(id+"F20.wireOp",EDGE,"E64.left")])]})});var subQ2=makeQuery(id+"F24.imprint","INTERSECT",VERTEX,{"disambiguationData":[OD(0.0)],"derivedFrom":[subQ1,subQ0]});Q3=makeQuery(id+"F24.imprint","IMPRINT",FACE,{"disambiguationData":[TD([[makeQuery(id+"F24.imprint","IMPRINT",EDGE,{"disambiguationData":[TD([[subQ2,1.0]])],"derivedFrom":subQ0}),1.0]])]});}
            var Q4;
            {var subQ0=sQuery(id+"F24.wireOp",EDGE,"E75.0.0");var subQ1=makeQuery(id+"F21.boolean.opBoolean","COPY",EDGE,{"derivedFrom":makeQuery(id+"F21.opExtrude","SWEPT_EDGE",EDGE,{"disambiguationData":[OSD([sQuery(id+"F18.wireOp",EDGE,"E62.bottom"),sQuery(id+"F18.wireOp",EDGE,"E62.right"),sQuery(id+"F20.wireOp",EDGE,"E64.bottom"),sQuery(id+"F20.wireOp",EDGE,"E64.left")])]})});var subQ2=makeQuery(id+"F24.imprint","INTERSECT",VERTEX,{"disambiguationData":[OD(0.0)],"derivedFrom":[subQ1,subQ0]});Q4=makeQuery(id+"F24.imprint","IMPRINT",FACE,{"disambiguationData":[TD([[makeQuery(id+"F24.imprint","IMPRINT",EDGE,{"disambiguationData":[TD([[subQ2,1.0]])],"derivedFrom":subQ0}),1.0]])]});}
            var Q5;
            {var subQ0=sQuery(id+"F24.wireOp",EDGE,"E75.0.0");var subQ1=makeQuery(id+"F21.boolean.opBoolean","COPY",EDGE,{"derivedFrom":makeQuery(id+"F21.opExtrude","SWEPT_EDGE",EDGE,{"disambiguationData":[OSD([sQuery(id+"F18.wireOp",EDGE,"E62.bottom"),sQuery(id+"F18.wireOp",EDGE,"E62.right"),sQuery(id+"F20.wireOp",EDGE,"E64.bottom"),sQuery(id+"F20.wireOp",EDGE,"E64.left")])]})});var subQ2=makeQuery(id+"F24.imprint","INTERSECT",VERTEX,{"disambiguationData":[OD(0.0)],"derivedFrom":[subQ1,subQ0]});Q5=makeQuery(id+"F24.imprint","IMPRINT",FACE,{"disambiguationData":[TD([[makeQuery(id+"F24.imprint","IMPRINT",EDGE,{"disambiguationData":[TD([[subQ2,-1.0]])],"derivedFrom":subQ0}),1.0]])]});}
            var Q6;
            {var subQ0=sQuery(id+"F24.wireOp",EDGE,"E76.0.0");var subQ1=makeQuery(id+"F21.boolean.opBoolean","COPY",EDGE,{"derivedFrom":makeQuery(id+"F21.opExtrude","SWEPT_EDGE",EDGE,{"disambiguationData":[OSD([sQuery(id+"F18.wireOp",EDGE,"E62.bottom"),sQuery(id+"F18.wireOp",EDGE,"E62.right"),sQuery(id+"F20.wireOp",EDGE,"E64.bottom"),sQuery(id+"F20.wireOp",EDGE,"E64.left")])]})});var subQ2=makeQuery(id+"F24.imprint","INTERSECT",VERTEX,{"disambiguationData":[OD(0.0)],"derivedFrom":[subQ1,subQ0]});Q6=makeQuery(id+"F24.imprint","IMPRINT",FACE,{"disambiguationData":[TD([[makeQuery(id+"F24.imprint","IMPRINT",EDGE,{"disambiguationData":[TD([[subQ2,1.0]])],"derivedFrom":subQ0}),1.0]])]});}
            var Q7;
            {var subQ0=sQuery(id+"F24.wireOp",EDGE,"E76.0.0");var subQ1=makeQuery(id+"F21.boolean.opBoolean","COPY",EDGE,{"derivedFrom":makeQuery(id+"F21.opExtrude","SWEPT_EDGE",EDGE,{"disambiguationData":[OSD([sQuery(id+"F18.wireOp",EDGE,"E62.bottom"),sQuery(id+"F18.wireOp",EDGE,"E62.right"),sQuery(id+"F20.wireOp",EDGE,"E64.bottom"),sQuery(id+"F20.wireOp",EDGE,"E64.left")])]})});var subQ2=makeQuery(id+"F24.imprint","INTERSECT",VERTEX,{"disambiguationData":[OD(0.0)],"derivedFrom":[subQ1,subQ0]});Q7=makeQuery(id+"F24.imprint","IMPRINT",FACE,{"disambiguationData":[TD([[makeQuery(id+"F24.imprint","IMPRINT",EDGE,{"disambiguationData":[TD([[subQ2,-1.0]])],"derivedFrom":subQ0}),1.0]])]});}
            extrude(context, id + "F25", {"entities" : qUnion([Q0, Q1, Q2, Q3, Q4, Q5, Q6, Q7]), "operationType" : NewBodyOperationType.REMOVE, "oppositeDirection" : true, "depth" : 29.2 * mm, "offsetDistance" : 25.4 * mm});
        }
        {
            var Q0;
            Q0=makeQuery(id+"F1.opExtrude","CAP_FACE",FACE,{"disambiguationData":[OSD([sQuery(id+"F0.wireOp",EDGE,"E0.bottom"),sQuery(id+"F0.wireOp",EDGE,"E0.top"),sQuery(id+"F0.wireOp",EDGE,"E0.left"),sQuery(id+"F0.wireOp",EDGE,"E0.right")])],"isStart":true});
            var sketch = newSketch(context, id + "F26", { "sketchPlane" : qUnion([Q0])});
            skCircle(sketch, "E77", {"center": v(0, 0) * mm, "radius": 50.8 * mm});
            skSolve(sketch);
        }
        {
            var Q0;
            Q0=makeQuery(id+"F26.imprint","IMPRINT",FACE,{"disambiguationData":[TD([[makeQuery(id+"F26.imprint","IMPRINT",EDGE,{"derivedFrom":sQuery(id+"F26.wireOp",EDGE,"E77")}),1.0]])]});
            extrude(context, id + "F27", {"entities" : qUnion([Q0]), "operationType" : NewBodyOperationType.REMOVE, "endBound" : BoundingType.THROUGH_ALL, "oppositeDirection" : true, "depth" : 25.4 * mm, "offsetDistance" : 25.4 * mm});
        }
        {
            var Q0;
            Q0=qCreatedBy(makeId("Right.planeOp"),FACE);
            var sketch = newSketch(context, id + "F28", { "sketchPlane" : qUnion([Q0])});
            skLineSegment(sketch, "E78.bottom", {"start": v(-373.82, 12.7) * mm, "end": v(-272.22, 12.7) * mm});
            skLineSegment(sketch, "E78.top", {"start": v(-373.82, -12.7) * mm, "end": v(-272.22, -12.7) * mm});
            skLineSegment(sketch, "E78.left", {"start": v(-373.82, 12.7) * mm, "end": v(-373.82, -12.7) * mm});
            skLineSegment(sketch, "E78.right", {"start": v(-272.22, 12.7) * mm, "end": v(-272.22, -12.7) * mm});
            skPoint(sketch, "E78.middle", {"position": v(-323.02, 0) * mm});
            skSolve(sketch);
        }
        {
            var Q0;
            Q0=makeQuery(id+"F28.imprint","IMPRINT",FACE,{"disambiguationData":[TD([[makeQuery(id+"F28.imprint","IMPRINT",EDGE,{"derivedFrom":sQuery(id+"F28.wireOp",EDGE,"E78.bottom")}),-1.0]])]});
            extrude(context, id + "F29", {"entities" : qUnion([Q0]), "endBound" : BoundingType.SYMMETRIC, "depth" : 44.45 * mm, "offsetDistance" : 25.4 * mm});
        }
        {
            var Q0;
            Q0=makeQuery(id+"F29.opExtrude","SWEPT_FACE",FACE,{"disambiguationData":[OSD([sQuery(id+"F28.wireOp",EDGE,"E78.bottom")])]});
            var sketch = newSketch(context, id + "F30", { "sketchPlane" : qUnion([Q0])});
            skPoint(sketch, "E79", {"position": v(0, -361.12) * mm});
            skPoint(sketch, "E79.positionSnap0", {"position": v(0, -373.82) * mm});
            skSolve(sketch);
        }
        {
            var Q0;
            Q0=sQuery(id+"F30.wireOp",VERTEX,"E79");
            var Q1;
            Q1=makeQuery(id+"F29.opExtrude","SWEPT_BODY",BODY,{"disambiguationData":[OSD([sQuery(id+"F28.wireOp",EDGE,"E78.bottom"),sQuery(id+"F28.wireOp",EDGE,"E78.top"),sQuery(id+"F28.wireOp",EDGE,"E78.left"),sQuery(id+"F28.wireOp",EDGE,"E78.right")])]});
            hole(context, id + "F31", {"style" : HoleStyle.SIMPLE, "endStyle" : HoleEndStyle.THROUGH, "standardTappedOrClearance" : lookupTablePath({ "standard" : "ANSI", "engagement" : "75%", "pitch" : "11 tpi", "size" : "5/8", "type" : "Tapped" }), "standardBlindInLast" : lookupTablePath({ "standard" : "ANSI", "fit" : "Free", "engagement" : "75%", "pitch" : "11 tpi", "size" : "5/8", "type" : "Clearance & tapped" }), "holeDiameter" : 13.5 * mm, "majorDiameter" : 15.88 * mm, "showTappedDepth" : true, "isTappedThrough" : true, "tappedDepth" : 21.59 * mm, "tapClearance" : 3, "startFromSketch" : true, "locations" : qUnion([Q0]), "scope" : qUnion([Q1])});
        }
        {
            var Q0;
            Q0=makeQuery(id+"F29.opExtrude","SWEPT_FACE",FACE,{"disambiguationData":[OSD([sQuery(id+"F28.wireOp",EDGE,"E78.bottom")])]});
            var sketch = newSketch(context, id + "F32", { "sketchPlane" : qUnion([Q0])});
            skLineSegment(sketch, "E80.bottom", {"start": v(-8.26, -272.22) * mm, "end": v(8.26, -272.22) * mm});
            skLineSegment(sketch, "E80.top", {"start": v(-8.25, -338.5) * mm, "end": v(8.25, -338.5) * mm});
            skLineSegment(sketch, "E80.left", {"start": v(-8.26, -272.22) * mm, "end": v(-8.25, -338.5) * mm});
            skLineSegment(sketch, "E80.right", {"start": v(8.26, -272.22) * mm, "end": v(8.26, -338.5) * mm});
            skPoint(sketch, "E81", {"position": v(0, -272.22) * mm});
            skArc(sketch, "E82", {"start": v(-8.25, -338.5) * mm, "mid": v(0, -346.76) * mm, "end": v(8.25, -338.5) * mm});
            skSolve(sketch);
        }
        {
            var Q0;
            Q0=makeQuery(id+"F32.imprint","IMPRINT",FACE,{"disambiguationData":[TD([[makeQuery(id+"F32.imprint","IMPRINT",EDGE,{"derivedFrom":sQuery(id+"F32.wireOp",EDGE,"E80.bottom")}),1.0]])]});
            var Q1;
            Q1=makeQuery(id+"F32.imprint","IMPRINT",FACE,{"disambiguationData":[TD([[makeQuery(id+"F32.imprint","IMPRINT",EDGE,{"derivedFrom":sQuery(id+"F32.wireOp",EDGE,"E80.top")}),-1.0]])]});
            extrude(context, id + "F33", {"entities" : qUnion([Q0, Q1]), "operationType" : NewBodyOperationType.REMOVE, "endBound" : BoundingType.THROUGH_ALL, "oppositeDirection" : true, "depth" : 25.4 * mm, "offsetDistance" : 25.4 * mm});
        }
        {
            var Q0;
            Q0=makeQuery(id+"F29.opExtrude","CAP_FACE",FACE,{"disambiguationData":[OSD([sQuery(id+"F28.wireOp",EDGE,"E78.bottom"),sQuery(id+"F28.wireOp",EDGE,"E78.top"),sQuery(id+"F28.wireOp",EDGE,"E78.left"),sQuery(id+"F28.wireOp",EDGE,"E78.right")])],"isStart":false});
            var sketch = newSketch(context, id + "F34", { "sketchPlane" : qUnion([Q0])});
            skLineSegment(sketch, "E83", {"start": v(-272.22, -3.18) * mm, "end": v(-288.1, -3.18) * mm});
            skLineSegment(sketch, "E84", {"start": v(-288.1, -3.18) * mm, "end": v(-291.27, -12.7) * mm});
            skSolve(sketch);
        }
        {
            var Q0;
            {var subQ0=sQuery(id+"F34.wireOp",EDGE,"E83");Q0=makeQuery(id+"F34.imprint","IMPRINT",FACE,{"disambiguationData":[TD([[makeQuery(id+"F34.imprint","IMPRINT",EDGE,{"derivedFrom":subQ0}),1.0]])]});}
            extrude(context, id + "F35", {"entities" : qUnion([Q0]), "operationType" : NewBodyOperationType.REMOVE, "endBound" : BoundingType.THROUGH_ALL, "oppositeDirection" : true, "depth" : 25.4 * mm, "offsetDistance" : 25.4 * mm});
        }
        {
            var Q0;
            Q0=makeQuery(id+"F29.opExtrude","CAP_FACE",FACE,{"disambiguationData":[OSD([sQuery(id+"F28.wireOp",EDGE,"E78.bottom"),sQuery(id+"F28.wireOp",EDGE,"E78.top"),sQuery(id+"F28.wireOp",EDGE,"E78.left"),sQuery(id+"F28.wireOp",EDGE,"E78.right")])],"isStart":false});
            var sketch = newSketch(context, id + "F36", { "sketchPlane" : qUnion([Q0])});
            skLineSegment(sketch, "E85.bottom", {"start": v(-272.22, 12.7) * mm, "end": v(-348.42, 12.7) * mm});
            skLineSegment(sketch, "E85.top", {"start": v(-272.22, 7.62) * mm, "end": v(-348.42, 7.62) * mm});
            skLineSegment(sketch, "E85.left", {"start": v(-272.22, 12.7) * mm, "end": v(-272.22, 7.62) * mm});
            skLineSegment(sketch, "E85.right", {"start": v(-348.42, 12.7) * mm, "end": v(-348.42, 7.62) * mm});
            skSolve(sketch);
        }
        {
            var Q0;
            Q0=makeQuery(id+"F36.imprint","IMPRINT",FACE,{"disambiguationData":[TD([[makeQuery(id+"F36.imprint","IMPRINT",EDGE,{"derivedFrom":sQuery(id+"F36.wireOp",EDGE,"E85.bottom")}),-1.0]])]});
            extrude(context, id + "F37", {"entities" : qUnion([Q0]), "operationType" : NewBodyOperationType.REMOVE, "endBound" : BoundingType.THROUGH_ALL, "oppositeDirection" : true, "depth" : 25.4 * mm, "offsetDistance" : 25.4 * mm});
        }
        {
            var Q0;
            Q0=makeQuery(id+"F29.opExtrude","CAP_FACE",FACE,{"disambiguationData":[OSD([sQuery(id+"F28.wireOp",EDGE,"E78.bottom"),sQuery(id+"F28.wireOp",EDGE,"E78.top"),sQuery(id+"F28.wireOp",EDGE,"E78.left"),sQuery(id+"F28.wireOp",EDGE,"E78.right")])],"isStart":false});
            cPlane(context, id + "F38", {"entities" : qUnion([Q0]), "cplaneType" : CPlaneType.OFFSET, "offset" : 25.4 * mm, "width" : 152.4 * mm, "height" : 152.4 * mm});
        }
        {
            var Q0;
            Q0=qCreatedBy(id+"F38.planeOp",FACE);
            var sketch = newSketch(context, id + "F39", { "sketchPlane" : qUnion([Q0])});
            skLineSegment(sketch, "E86.0.0", {"start": v(-348.42, 7.62) * mm, "end": v(-348.42, 12.7) * mm});
            skLineSegment(sketch, "E86.0.1", {"start": v(-348.42, 12.7) * mm, "end": v(-373.82, 12.7) * mm});
            skLineSegment(sketch, "E86.0.2", {"start": v(-373.82, 12.7) * mm, "end": v(-373.82, -12.7) * mm});
            skLineSegment(sketch, "E86.0.3", {"start": v(-373.82, -12.7) * mm, "end": v(-291.27, -12.7) * mm});
            skLineSegment(sketch, "E86.0.4", {"start": v(-291.27, -12.7) * mm, "end": v(-288.1, -3.18) * mm});
            skLineSegment(sketch, "E86.0.5", {"start": v(-288.1, -3.18) * mm, "end": v(-272.22, -3.18) * mm});
            skLineSegment(sketch, "E86.0.6", {"start": v(-272.22, -3.18) * mm, "end": v(-272.22, 7.62) * mm});
            skLineSegment(sketch, "E86.0.7", {"start": v(-272.22, 7.62) * mm, "end": v(-348.42, 7.62) * mm});
            skSolve(sketch);
        }
        {
            var Q0;
            Q0=makeQuery(id+"F39.imprint","IMPRINT",FACE,{"disambiguationData":[TD([[makeQuery(id+"F39.imprint","IMPRINT",EDGE,{"derivedFrom":sQuery(id+"F39.wireOp",EDGE,"E86.0.0")}),1.0]])]});
            extrude(context, id + "F40", {"entities" : qUnion([Q0]), "depth" : 88.9 * mm, "offsetDistance" : 25.4 * mm});
        }
        {
            var Q0;
            Q0=makeQuery(id+"F40.opExtrude","SWEPT_FACE",FACE,{"disambiguationData":[OSD([sQuery(id+"F39.wireOp",EDGE,"E86.0.1")])]});
            var sketch = newSketch(context, id + "F41", { "sketchPlane" : qUnion([Q0])});
            skPoint(sketch, "E87", {"position": v(92.08, -361.12) * mm});
            skPoint(sketch, "E87.positionSnap0", {"position": v(47.62, -361.12) * mm});
            skPoint(sketch, "E87.positionSnap1", {"position": v(92.08, -373.82) * mm});
            skSolve(sketch);
        }
        {
            var Q0;
            Q0=sQuery(id+"F41.wireOp",VERTEX,"E87");
            var Q1;
            Q1=makeQuery(id+"F40.opExtrude","SWEPT_BODY",BODY,{"disambiguationData":[OSD([sQuery(id+"F39.wireOp",EDGE,"E86.0.0"),sQuery(id+"F39.wireOp",EDGE,"E86.0.1"),sQuery(id+"F39.wireOp",EDGE,"E86.0.2"),sQuery(id+"F39.wireOp",EDGE,"E86.0.3"),sQuery(id+"F39.wireOp",EDGE,"E86.0.4"),sQuery(id+"F39.wireOp",EDGE,"E86.0.5"),sQuery(id+"F39.wireOp",EDGE,"E86.0.6"),sQuery(id+"F39.wireOp",EDGE,"E86.0.7")])]});
            hole(context, id + "F42", {"style" : HoleStyle.SIMPLE, "endStyle" : HoleEndStyle.THROUGH, "standardTappedOrClearance" : lookupTablePath({ "standard" : "ANSI", "engagement" : "75%", "pitch" : "11 tpi", "size" : "5/8", "type" : "Tapped" }), "standardBlindInLast" : lookupTablePath({ "standard" : "ANSI", "fit" : "Free", "engagement" : "75%", "pitch" : "11 tpi", "size" : "5/8", "type" : "Clearance & tapped" }), "holeDiameter" : 13.5 * mm, "majorDiameter" : 15.88 * mm, "showTappedDepth" : true, "isTappedThrough" : true, "tappedDepth" : 21.59 * mm, "tapClearance" : 3, "startFromSketch" : true, "locations" : qUnion([Q0]), "scope" : qUnion([Q1])});
        }
        {
            var Q0;
            Q0=makeQuery(id+"F40.opExtrude","SWEPT_FACE",FACE,{"disambiguationData":[OSD([sQuery(id+"F39.wireOp",EDGE,"E86.0.7")])]});
            var sketch = newSketch(context, id + "F43", { "sketchPlane" : qUnion([Q0])});
            skLineSegment(sketch, "E88.bottom", {"start": v(58.42, -272.22) * mm, "end": v(74.93, -272.22) * mm});
            skLineSegment(sketch, "E88.top", {"start": v(58.42, -323.02) * mm, "end": v(74.93, -323.02) * mm});
            skLineSegment(sketch, "E88.left", {"start": v(58.42, -272.22) * mm, "end": v(58.42, -323.02) * mm});
            skLineSegment(sketch, "E88.right", {"start": v(74.93, -272.22) * mm, "end": v(74.93, -323.02) * mm});
            skArc(sketch, "E89", {"start": v(58.42, -323.02) * mm, "mid": v(66.67, -331.28) * mm, "end": v(74.93, -323.02) * mm});
            skLineSegment(sketch, "E90.bottom", {"start": v(109.22, -272.22) * mm, "end": v(125.73, -272.22) * mm});
            skLineSegment(sketch, "E90.top", {"start": v(109.22, -323.02) * mm, "end": v(125.73, -323.02) * mm});
            skLineSegment(sketch, "E90.left", {"start": v(109.22, -272.22) * mm, "end": v(109.22, -323.02) * mm});
            skLineSegment(sketch, "E90.right", {"start": v(125.73, -272.22) * mm, "end": v(125.73, -323.02) * mm});
            skArc(sketch, "E91", {"start": v(109.22, -323.02) * mm, "mid": v(117.48, -331.28) * mm, "end": v(125.73, -323.02) * mm});
            skLineSegment(sketch, "E92", {"start": v(74.93, -323.02) * mm, "end": v(109.22, -323.02) * mm, "construction": true});
            skPoint(sketch, "E93", {"position": v(92.08, -323.02) * mm});
            skPoint(sketch, "E94", {"position": v(92.08, -272.22) * mm});
            skSolve(sketch);
        }
        {
            var Q0;
            Q0=makeQuery(id+"F43.imprint","IMPRINT",FACE,{"disambiguationData":[TD([[makeQuery(id+"F43.imprint","IMPRINT",EDGE,{"derivedFrom":sQuery(id+"F43.wireOp",EDGE,"E88.bottom")}),1.0]])]});
            var Q1;
            Q1=makeQuery(id+"F43.imprint","IMPRINT",FACE,{"disambiguationData":[TD([[makeQuery(id+"F43.imprint","IMPRINT",EDGE,{"derivedFrom":sQuery(id+"F43.wireOp",EDGE,"E88.top")}),-1.0]])]});
            var Q2;
            Q2=makeQuery(id+"F43.imprint","IMPRINT",FACE,{"disambiguationData":[TD([[makeQuery(id+"F43.imprint","IMPRINT",EDGE,{"derivedFrom":sQuery(id+"F43.wireOp",EDGE,"E90.top")}),-1.0]])]});
            var Q3;
            Q3=makeQuery(id+"F43.imprint","IMPRINT",FACE,{"disambiguationData":[TD([[makeQuery(id+"F43.imprint","IMPRINT",EDGE,{"derivedFrom":sQuery(id+"F43.wireOp",EDGE,"E90.bottom")}),1.0]])]});
            extrude(context, id + "F44", {"entities" : qUnion([Q0, Q1, Q2, Q3]), "operationType" : NewBodyOperationType.REMOVE, "endBound" : BoundingType.THROUGH_ALL, "oppositeDirection" : true, "depth" : 25.4 * mm, "offsetDistance" : 25.4 * mm});
        }
        {
            var Q0;
            Q0=makeQuery(id+"F40.opExtrude","SWEPT_FACE",FACE,{"disambiguationData":[OSD([sQuery(id+"F39.wireOp",EDGE,"E86.0.7")])]});
            var sketch = newSketch(context, id + "F45", { "sketchPlane" : qUnion([Q0])});
            skLineSegment(sketch, "E95.0", {"start": v(58.42, -272.22) * mm, "end": v(58.42, -323.02) * mm});
            skLineSegment(sketch, "E96.0", {"start": v(74.93, -272.22) * mm, "end": v(74.93, -323.02) * mm});
            skLineSegment(sketch, "E97.0", {"start": v(109.22, -272.22) * mm, "end": v(109.22, -323.02) * mm});
            skLineSegment(sketch, "E98.0", {"start": v(125.73, -272.22) * mm, "end": v(125.73, -323.02) * mm});
            skLineSegment(sketch, "E99", {"start": v(58.42, -272.22) * mm, "end": v(74.93, -272.22) * mm});
            skLineSegment(sketch, "E100", {"start": v(109.22, -272.22) * mm, "end": v(125.73, -272.22) * mm});
            skArc(sketch, "E101", {"start": v(74.93, -294.45) * mm, "mid": v(66.67, -286.2) * mm, "end": v(58.42, -294.45) * mm});
            skPoint(sketch, "E102", {"position": v(66.67, -272.22) * mm});
            skPoint(sketch, "E103", {"position": v(117.48, -272.22) * mm});
            skArc(sketch, "E104", {"start": v(125.73, -294.45) * mm, "mid": v(117.48, -286.2) * mm, "end": v(109.22, -294.45) * mm});
            skSolve(sketch);
        }
        {
            var Q0;
            {var subQ0=sQuery(id+"F45.wireOp",EDGE,"E99");Q0=makeQuery(id+"F45.imprint","IMPRINT",FACE,{"disambiguationData":[TD([[makeQuery(id+"F45.imprint","IMPRINT",EDGE,{"derivedFrom":subQ0}),-1.0]])]});}
            var Q1;
            {var subQ0=sQuery(id+"F45.wireOp",EDGE,"E100");Q1=makeQuery(id+"F45.imprint","IMPRINT",FACE,{"disambiguationData":[TD([[makeQuery(id+"F45.imprint","IMPRINT",EDGE,{"derivedFrom":subQ0}),-1.0]])]});}
            var Q2;
            Q2=makeQuery(id+"F40.opExtrude","SWEPT_FACE",FACE,{"disambiguationData":[OSD([sQuery(id+"F39.wireOp",EDGE,"E86.0.3")])]});
            extrude(context, id + "F46", {"entities" : qUnion([Q0, Q1]), "operationType" : NewBodyOperationType.ADD, "endBound" : BoundingType.UP_TO_SURFACE, "oppositeDirection" : true, "depth" : 25.4 * mm, "endBoundEntityFace" : qUnion([Q2]), "offsetDistance" : 25.4 * mm});
        }
        {
            var Q0;
            Q0=makeQuery(id+"F40.opExtrude","CAP_EDGE",EDGE,{"disambiguationData":[OSD([sQuery(id+"F39.wireOp",EDGE,"E86.0.6")])],"isStart":false});
            var Q1;
            Q1=makeQuery(id+"F40.opExtrude","CAP_EDGE",EDGE,{"disambiguationData":[OSD([sQuery(id+"F39.wireOp",EDGE,"E86.0.6")])],"isStart":true});
            chamfer(context, id + "F47", {"entities" : qUnion([Q0, Q1]), "width" : 22.22 * mm});
        }
        {
            var Q0;
            Q0=makeQuery(id+"F40.opExtrude","CAP_FACE",FACE,{"disambiguationData":[OSD([sQuery(id+"F39.wireOp",EDGE,"E86.0.0"),sQuery(id+"F39.wireOp",EDGE,"E86.0.1"),sQuery(id+"F39.wireOp",EDGE,"E86.0.2"),sQuery(id+"F39.wireOp",EDGE,"E86.0.3"),sQuery(id+"F39.wireOp",EDGE,"E86.0.4"),sQuery(id+"F39.wireOp",EDGE,"E86.0.5"),sQuery(id+"F39.wireOp",EDGE,"E86.0.6"),sQuery(id+"F39.wireOp",EDGE,"E86.0.7")])],"isStart":false});
            var sketch = newSketch(context, id + "F48", { "sketchPlane" : qUnion([Q0])});
            skLineSegment(sketch, "E105.bottom", {"start": v(-348.42, 12.7) * mm, "end": v(-373.82, 12.7) * mm});
            skLineSegment(sketch, "E105.top", {"start": v(-348.42, 7.62) * mm, "end": v(-373.82, 7.62) * mm});
            skLineSegment(sketch, "E105.left", {"start": v(-348.42, 12.7) * mm, "end": v(-348.42, 7.62) * mm});
            skLineSegment(sketch, "E105.right", {"start": v(-373.82, 12.7) * mm, "end": v(-373.82, 7.62) * mm});
            skSolve(sketch);
        }
        {
            var Q0;
            Q0=makeQuery(id+"F48.imprint","IMPRINT",FACE,{"disambiguationData":[TD([[makeQuery(id+"F48.imprint","IMPRINT",EDGE,{"derivedFrom":sQuery(id+"F48.wireOp",EDGE,"E105.bottom")}),1.0]])]});
            extrude(context, id + "F49", {"entities" : qUnion([Q0]), "operationType" : NewBodyOperationType.REMOVE, "endBound" : BoundingType.THROUGH_ALL, "oppositeDirection" : true, "depth" : 25.4 * mm, "offsetDistance" : 25.4 * mm});
        }
        {
            var Q0;
            Q0=makeQuery(id+"F46.opExtrude","SWEPT_FACE",FACE,{"disambiguationData":[OSD([sQuery(id+"F45.wireOp",EDGE,"E98.0")])]});
            var sketch = newSketch(context, id + "F50", { "sketchPlane" : qUnion([Q0])});
            skLineSegment(sketch, "E106", {"start": v(-288.1, -3.18) * mm, "end": v(-291.27, -12.7) * mm});
            skLineSegment(sketch, "E107", {"start": v(-291.27, -12.7) * mm, "end": v(-272.22, -12.7) * mm});
            skLineSegment(sketch, "E108", {"start": v(-272.22, -12.7) * mm, "end": v(-272.22, -3.18) * mm});
            skLineSegment(sketch, "E109", {"start": v(-272.22, -3.18) * mm, "end": v(-288.1, -3.18) * mm});
            skLineSegment(sketch, "E110.0", {"start": v(-272.22, 7.62) * mm, "end": v(-272.22, -12.7) * mm});
            skSolve(sketch);
        }
        {
            var Q0;
            {var subQ1=makeQuery(id+"F47.opChamfer","BLEND_EDGE",EDGE,{"blendedFrom":[makeQuery(id+"F40.opExtrude","CAP_EDGE",EDGE,{"disambiguationData":[OSD([sQuery(id+"F39.wireOp",EDGE,"E86.0.6")])],"isStart":false}),makeQuery(id+"F46.opExtrude","SWEPT_FACE",FACE,{"disambiguationData":[OSD([sQuery(id+"F45.wireOp",EDGE,"E98.0")])]})],"blendedInto":[makeQuery(id+"F46.opExtrude","SWEPT_FACE",FACE,{"disambiguationData":[OSD([sQuery(id+"F45.wireOp",EDGE,"E98.0")])]})]});Q0=makeQuery(id+"F50.imprint","IMPRINT",FACE,{"disambiguationData":[TD([[makeQuery(id+"F50.imprint","IMPRINT",EDGE,{"derivedFrom":subQ1}),-1.0]])]});}
            var Q1;
            {var subQ0=sQuery(id+"F50.wireOp",EDGE,"E106");Q1=makeQuery(id+"F50.imprint","IMPRINT",FACE,{"disambiguationData":[TD([[makeQuery(id+"F50.imprint","IMPRINT",EDGE,{"derivedFrom":subQ0}),1.0]])]});}
            extrude(context, id + "F51", {"entities" : qUnion([Q0, Q1]), "operationType" : NewBodyOperationType.REMOVE, "endBound" : BoundingType.THROUGH_ALL, "oppositeDirection" : true, "depth" : 25.4 * mm, "offsetDistance" : 25.4 * mm});
        }
        {
            var Q0;
            Q0=qCreatedBy(makeId("Right.planeOp"),FACE);
            var sketch = newSketch(context, id + "F52", { "sketchPlane" : qUnion([Q0])});
            skLineSegment(sketch, "E111.bottom", {"start": v(-340.5, 113.22) * mm, "end": v(-219.85, 113.22) * mm});
            skLineSegment(sketch, "E111.top", {"start": v(-340.5, 75.28) * mm, "end": v(-219.85, 75.28) * mm});
            skLineSegment(sketch, "E111.left", {"start": v(-340.5, 113.22) * mm, "end": v(-340.5, 75.28) * mm});
            skLineSegment(sketch, "E111.right", {"start": v(-219.85, 113.22) * mm, "end": v(-219.85, 75.28) * mm});
            skSolve(sketch);
        }
        {
            var Q0;
            Q0=makeQuery(id+"F52.imprint","IMPRINT",FACE,{"disambiguationData":[TD([[makeQuery(id+"F52.imprint","IMPRINT",EDGE,{"derivedFrom":sQuery(id+"F52.wireOp",EDGE,"E111.bottom")}),-1.0]])]});
            extrude(context, id + "F53", {"entities" : qUnion([Q0]), "endBound" : BoundingType.SYMMETRIC, "depth" : 50.8 * mm, "offsetDistance" : 25.4 * mm});
        }
        {
            var Q0;
            Q0=makeQuery(id+"F53.opExtrude","CAP_FACE",FACE,{"disambiguationData":[OSD([sQuery(id+"F52.wireOp",EDGE,"E111.bottom"),sQuery(id+"F52.wireOp",EDGE,"E111.top"),sQuery(id+"F52.wireOp",EDGE,"E111.left"),sQuery(id+"F52.wireOp",EDGE,"E111.right")])],"isStart":false});
            var sketch = newSketch(context, id + "F54", { "sketchPlane" : qUnion([Q0])});
            skLineSegment(sketch, "E112", {"start": v(-340.5, 97.73) * mm, "end": v(-321.45, 97.73) * mm});
            skLineSegment(sketch, "E113", {"start": v(-321.45, 97.73) * mm, "end": v(-317.64, 80.04) * mm});
            skLineSegment(sketch, "E114", {"start": v(-317.64, 80.04) * mm, "end": v(-252.87, 80.04) * mm});
            skLineSegment(sketch, "E115", {"start": v(-252.87, 80.04) * mm, "end": v(-252.87, 75.28) * mm});
            skLineSegment(sketch, "E116", {"start": v(-252.87, 75.28) * mm, "end": v(-340.5, 75.28) * mm});
            skLineSegment(sketch, "E117", {"start": v(-340.5, 75.28) * mm, "end": v(-340.5, 97.73) * mm});
            skSolve(sketch);
        }
        {
            var Q0;
            Q0=makeQuery(id+"F54.imprint","IMPRINT",FACE,{"disambiguationData":[TD([[makeQuery(id+"F54.imprint","IMPRINT",EDGE,{"derivedFrom":sQuery(id+"F54.wireOp",EDGE,"E112")}),-1.0]])]});
            extrude(context, id + "F55", {"entities" : qUnion([Q0]), "operationType" : NewBodyOperationType.REMOVE, "endBound" : BoundingType.THROUGH_ALL, "oppositeDirection" : true, "depth" : 25.4 * mm, "offsetDistance" : 25.4 * mm});
        }
        {
            var Q0;
            Q0=makeQuery(id+"F53.opExtrude","SWEPT_FACE",FACE,{"disambiguationData":[OSD([sQuery(id+"F52.wireOp",EDGE,"E111.bottom")])]});
            var sketch = newSketch(context, id + "F56", { "sketchPlane" : qUnion([Q0])});
            skCircle(sketch, "E118", {"center": v(0, -265.03) * mm, "radius": 10 * mm});
            skPoint(sketch, "E118.centerSnap0", {"position": v(0, -340.5) * mm});
            skLineSegment(sketch, "E119", {"start": v(-10, -265.03) * mm, "end": v(-10, -340.5) * mm});
            skLineSegment(sketch, "E120", {"start": v(10, -265.03) * mm, "end": v(10, -340.5) * mm});
            skSolve(sketch);
        }
        {
            var Q0;
            {var subQ0=sQuery(id+"F56.wireOp",EDGE,"E119");Q0=makeQuery(id+"F56.imprint","IMPRINT",FACE,{"disambiguationData":[TD([[makeQuery(id+"F56.imprint","IMPRINT",EDGE,{"derivedFrom":subQ0}),1.0]])]});}
            var Q1;
            {var subQ0=sQuery(id+"F56.wireOp",EDGE,"E118");var subQ1=makeQuery(id+"F56.imprint","INTERSECT",VERTEX,{"derivedFrom":[subQ0,sQuery(id+"F56.wireOp",EDGE,"E119")]});Q1=makeQuery(id+"F56.imprint","IMPRINT",FACE,{"disambiguationData":[TD([[makeQuery(id+"F56.imprint","IMPRINT",EDGE,{"disambiguationData":[TD([[subQ1,1.0]])],"derivedFrom":subQ0}),1.0]])]});}
            extrude(context, id + "F57", {"entities" : qUnion([Q0, Q1]), "operationType" : NewBodyOperationType.REMOVE, "endBound" : BoundingType.THROUGH_ALL, "oppositeDirection" : true, "depth" : 25.4 * mm, "offsetDistance" : 25.4 * mm});
        }
        {
            var Q0;
            Q0=makeQuery(id+"F53.opExtrude","SWEPT_FACE",FACE,{"disambiguationData":[OSD([sQuery(id+"F52.wireOp",EDGE,"E111.bottom")])]});
            var sketch = newSketch(context, id + "F58", { "sketchPlane" : qUnion([Q0])});
            skPoint(sketch, "E121", {"position": v(0, -236.06) * mm});
            skPoint(sketch, "E121.positionSnap0", {"position": v(0, -219.85) * mm});
            skSolve(sketch);
        }
        {
            var Q0;
            Q0=sQuery(id+"F58.wireOp",VERTEX,"E121");
            var Q1;
            Q1=makeQuery(id+"F53.opExtrude","SWEPT_BODY",BODY,{"disambiguationData":[OSD([sQuery(id+"F52.wireOp",EDGE,"E111.bottom"),sQuery(id+"F52.wireOp",EDGE,"E111.top"),sQuery(id+"F52.wireOp",EDGE,"E111.left"),sQuery(id+"F52.wireOp",EDGE,"E111.right")])]});
            hole(context, id + "F59", {"style" : HoleStyle.SIMPLE, "endStyle" : HoleEndStyle.THROUGH, "standardTappedOrClearance" : lookupTablePath({ "standard" : "ANSI", "engagement" : "75%", "pitch" : "10 tpi", "size" : "3/4", "type" : "Tapped" }), "standardBlindInLast" : lookupTablePath({ "standard" : "ANSI", "fit" : "Free", "engagement" : "75%", "pitch" : "10 tpi", "size" : "3/4", "type" : "Clearance & tapped" }), "holeDiameter" : 16.67 * mm, "majorDiameter" : 19.05 * mm, "showTappedDepth" : true, "isTappedThrough" : true, "tappedDepth" : 31.17 * mm, "tapClearance" : 3, "startFromSketch" : true, "locations" : qUnion([Q0]), "scope" : qUnion([Q1])});
        }
        {
            var Q0;
            Q0=makeQuery(id+"F53.opExtrude","CAP_FACE",FACE,{"disambiguationData":[OSD([sQuery(id+"F52.wireOp",EDGE,"E111.bottom"),sQuery(id+"F52.wireOp",EDGE,"E111.top"),sQuery(id+"F52.wireOp",EDGE,"E111.left"),sQuery(id+"F52.wireOp",EDGE,"E111.right")])],"isStart":false});
            var sketch = newSketch(context, id + "F60", { "sketchPlane" : qUnion([Q0])});
            skLineSegment(sketch, "E122.bottom", {"start": v(-340.5, 113.22) * mm, "end": v(-252.87, 113.22) * mm});
            skLineSegment(sketch, "E122.top", {"start": v(-340.5, 108.14) * mm, "end": v(-252.87, 108.14) * mm});
            skLineSegment(sketch, "E122.left", {"start": v(-340.5, 113.22) * mm, "end": v(-340.5, 108.14) * mm});
            skLineSegment(sketch, "E122.right", {"start": v(-252.87, 113.22) * mm, "end": v(-252.87, 108.14) * mm});
            skSolve(sketch);
        }
        {
            var Q0;
            Q0=makeQuery(id+"F60.imprint","IMPRINT",FACE,{"disambiguationData":[TD([[makeQuery(id+"F60.imprint","IMPRINT",EDGE,{"derivedFrom":sQuery(id+"F60.wireOp",EDGE,"E122.bottom")}),-1.0]])]});
            extrude(context, id + "F61", {"entities" : qUnion([Q0]), "operationType" : NewBodyOperationType.REMOVE, "endBound" : BoundingType.THROUGH_ALL, "oppositeDirection" : true, "depth" : 25.4 * mm, "offsetDistance" : 25.4 * mm});
        }
    });
